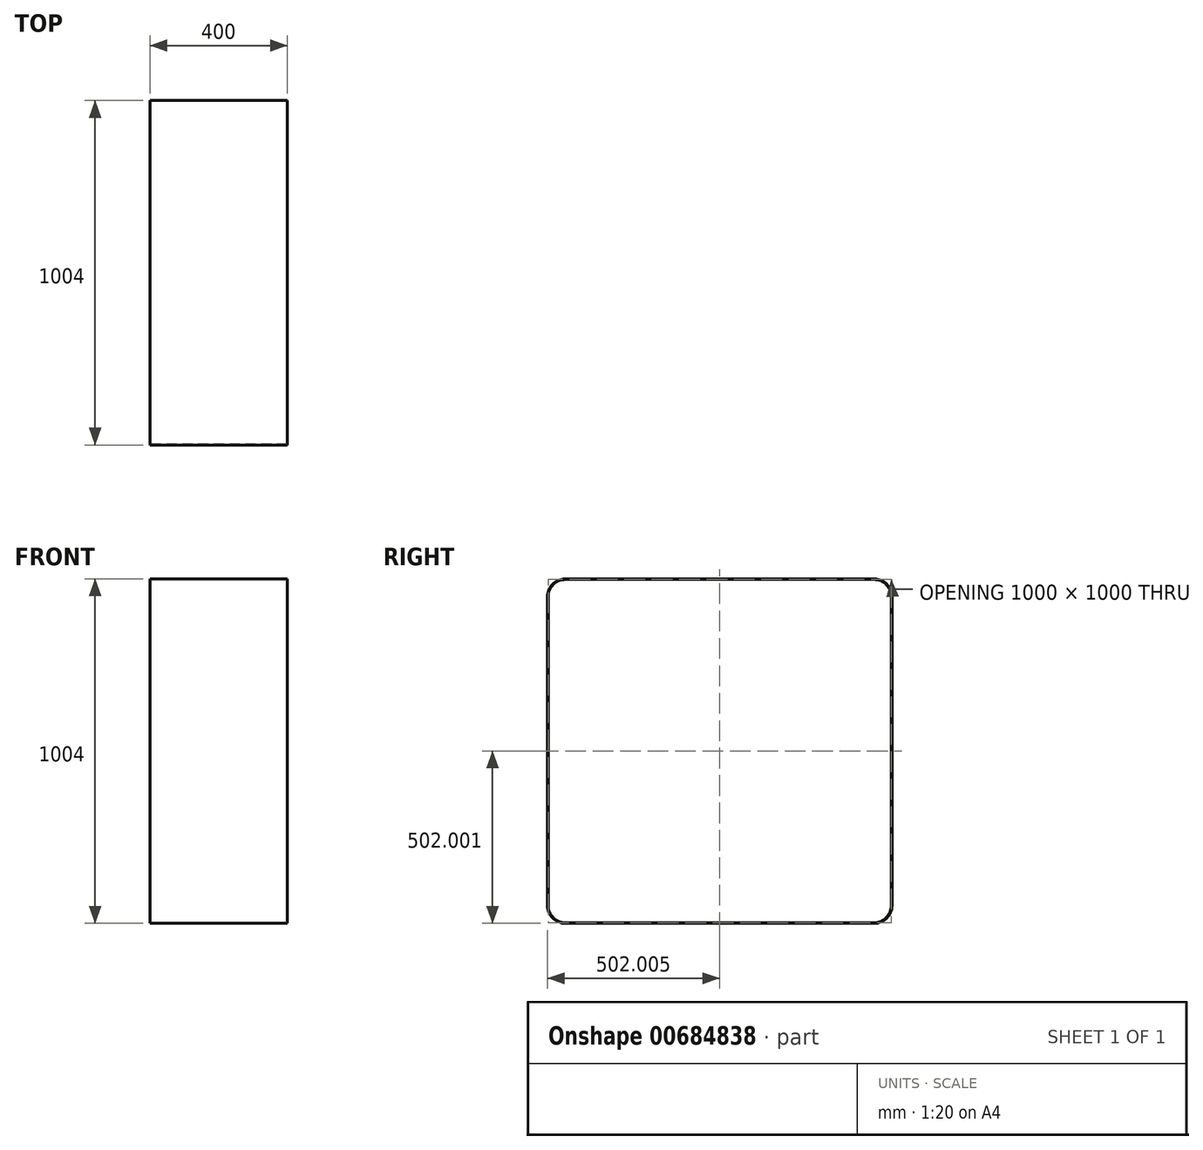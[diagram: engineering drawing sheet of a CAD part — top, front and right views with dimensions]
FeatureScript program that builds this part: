
annotation { "Feature Type Name" : "Feature", "Feature Type Description" : "" }
export const myFeature = defineFeature(function(context is Context, id is Id, definition is map)
    precondition{}
    {
        {
            var Q0;
            Q0=qCreatedBy(makeId("Right.planeOp"),FACE);
            var sketch = newSketch(context, id + "F0", { "sketchPlane" : qUnion([Q0])});
            skLineSegment(sketch, "E0.bottom", {"start": v(9.91, 900.88) * mm, "end": v(909.91, 900.88) * mm});
            skLineSegment(sketch, "E0.top", {"start": v(9.91, -99.12) * mm, "end": v(909.91, -99.12) * mm});
            skLineSegment(sketch, "E0.left", {"start": v(-40.09, 850.88) * mm, "end": v(-40.09, -49.12) * mm});
            skLineSegment(sketch, "E0.right", {"start": v(959.91, 850.88) * mm, "end": v(959.91, -49.12) * mm});
            skPoint(sketch, "E1.visualSharp", {"position": v(-40.09, -99.12) * mm});
            skArc(sketch, "E1.filletArc", {"start": v(-40.09, -49.12) * mm, "mid": v(-25.44, -84.47) * mm, "end": v(9.91, -99.12) * mm});
            skPoint(sketch, "E2.visualSharp", {"position": v(959.91, -99.12) * mm});
            skArc(sketch, "E2.filletArc", {"start": v(909.91, -99.12) * mm, "mid": v(945.27, -84.47) * mm, "end": v(959.91, -49.12) * mm});
            skPoint(sketch, "E3.visualSharp", {"position": v(-40.09, 900.88) * mm});
            skArc(sketch, "E3.filletArc", {"start": v(9.91, 900.88) * mm, "mid": v(-25.44, 886.24) * mm, "end": v(-40.09, 850.88) * mm});
            skPoint(sketch, "E4.visualSharp", {"position": v(959.91, 900.88) * mm});
            skArc(sketch, "E4.filletArc", {"start": v(959.91, 850.88) * mm, "mid": v(945.27, 886.24) * mm, "end": v(909.91, 900.88) * mm});
            skArc(sketch, "E5.0", {"start": v(-42.09, -49.12) * mm, "mid": v(-26.85, -85.89) * mm, "end": v(9.91, -101.12) * mm});
            skLineSegment(sketch, "E5.1", {"start": v(-42.09, 850.88) * mm, "end": v(-42.09, -49.12) * mm});
            skLineSegment(sketch, "E5.2", {"start": v(9.91, -101.12) * mm, "end": v(909.91, -101.12) * mm});
            skArc(sketch, "E5.3", {"start": v(9.91, 902.88) * mm, "mid": v(-26.85, 887.65) * mm, "end": v(-42.09, 850.88) * mm});
            skArc(sketch, "E5.4", {"start": v(909.91, -101.12) * mm, "mid": v(946.68, -85.89) * mm, "end": v(961.91, -49.12) * mm});
            skLineSegment(sketch, "E5.5", {"start": v(961.91, 850.88) * mm, "end": v(961.91, -49.12) * mm});
            skArc(sketch, "E5.6", {"start": v(961.91, 850.88) * mm, "mid": v(946.68, 887.65) * mm, "end": v(909.91, 902.88) * mm});
            skLineSegment(sketch, "E5.7", {"start": v(9.91, 902.88) * mm, "end": v(909.91, 902.88) * mm});
            skSolve(sketch);
        }
        {
            var Q0;
            Q0=makeQuery(id+"F0.imprint","IMPRINT",FACE,{"disambiguationData":[TD([[makeQuery(id+"F0.imprint","IMPRINT",EDGE,{"derivedFrom":sQuery(id+"F0.wireOp",EDGE,"E0.bottom")}),1.0]])]});
            extrude(context, id + "F1", {"entities" : qUnion([Q0]), "depth" : 400 * mm, "offsetDistance" : 25 * mm});
        }
    });
